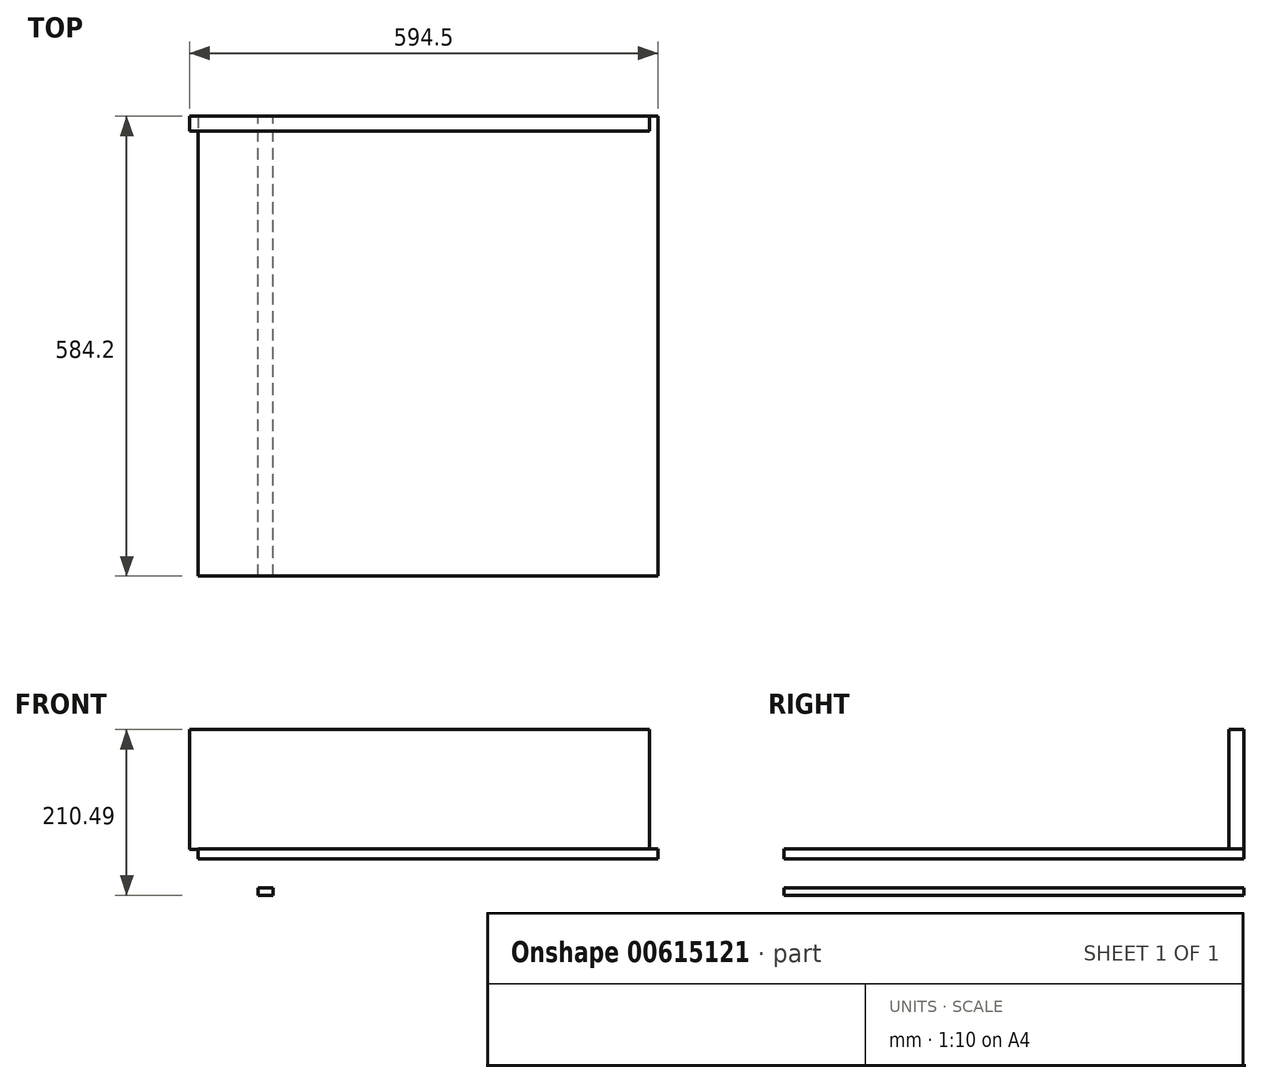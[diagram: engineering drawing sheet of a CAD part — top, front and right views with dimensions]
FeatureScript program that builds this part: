
annotation { "Feature Type Name" : "Feature", "Feature Type Description" : "" }
export const myFeature = defineFeature(function(context is Context, id is Id, definition is map)
    precondition{}
    {
        {
            var Q0;
            Q0=qCreatedBy(makeId("Front.planeOp"),FACE);
            var sketch = newSketch(context, id + "F0", { "sketchPlane" : qUnion([Q0])});
            skLineSegment(sketch, "E0.bottom", {"start": v(-279.42, 0.93) * mm, "end": v(304.78, 0.93) * mm});
            skLineSegment(sketch, "E0.top", {"start": v(-279.42, -11.77) * mm, "end": v(304.78, -11.77) * mm});
            skLineSegment(sketch, "E0.left", {"start": v(-279.42, 0.93) * mm, "end": v(-279.42, -11.77) * mm});
            skLineSegment(sketch, "E0.right", {"start": v(304.78, 0.93) * mm, "end": v(304.78, -11.77) * mm});
            skSolve(sketch);
        }
        {
            var Q0;
            Q0=qCreatedBy(makeId("Front.planeOp"),FACE);
            var sketch = newSketch(context, id + "F1", { "sketchPlane" : qUnion([Q0])});
            skLineSegment(sketch, "E1.bottom", {"start": v(-202.85, -48.57) * mm, "end": v(-183.8, -48.57) * mm});
            skLineSegment(sketch, "E1.top", {"start": v(-202.85, -58.1) * mm, "end": v(-183.8, -58.1) * mm});
            skLineSegment(sketch, "E1.left", {"start": v(-202.85, -48.57) * mm, "end": v(-202.85, -58.1) * mm});
            skLineSegment(sketch, "E1.right", {"start": v(-183.8, -48.57) * mm, "end": v(-183.8, -58.1) * mm});
            skSolve(sketch);
        }
        {
            var Q0;
            Q0=qSketchRegion(id+"F1",true);
            extrude(context, id + "F2", {"entities" : qUnion([Q0]), "depth" : 584.2 * mm});
        }
        {
            var Q0;
            Q0=qSketchRegion(id+"F0",true);
            extrude(context, id + "F3", {"entities" : qUnion([Q0]), "depth" : 584.2 * mm});
        }
        {
            var Q0;
            Q0=qCreatedBy(makeId("Front.planeOp"),FACE);
            var sketch = newSketch(context, id + "F4", { "sketchPlane" : qUnion([Q0])});
            skLineSegment(sketch, "E2.bottom", {"start": v(-289.72, 0) * mm, "end": v(294.48, 0) * mm});
            skLineSegment(sketch, "E2.top", {"start": v(-289.72, 152.4) * mm, "end": v(294.48, 152.4) * mm});
            skLineSegment(sketch, "E2.left", {"start": v(-289.72, 0) * mm, "end": v(-289.72, 152.4) * mm});
            skLineSegment(sketch, "E2.right", {"start": v(294.48, 0) * mm, "end": v(294.48, 152.4) * mm});
            skSolve(sketch);
        }
        {
            var Q0;
            Q0=qSketchRegion(id+"F4",true);
            extrude(context, id + "F5", {"entities" : qUnion([Q0]), "operationType" : NewBodyOperationType.ADD, "depth" : 19.05 * mm});
        }
    });
